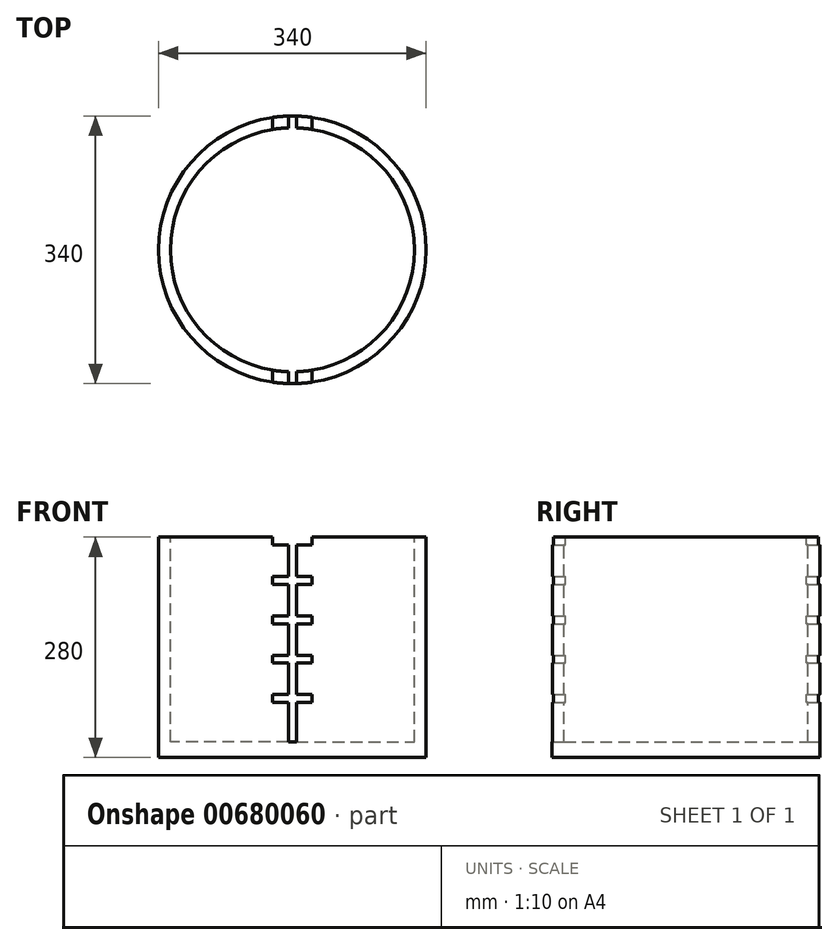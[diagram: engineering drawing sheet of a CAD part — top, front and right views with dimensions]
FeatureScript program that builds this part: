
annotation { "Feature Type Name" : "Feature", "Feature Type Description" : "" }
export const myFeature = defineFeature(function(context is Context, id is Id, definition is map)
    precondition{}
    {
        {
            var Q0;
            Q0=qCreatedBy(makeId("Top.planeOp"),FACE);
            var sketch = newSketch(context, id + "F0", { "sketchPlane" : qUnion([Q0])});
            skCircle(sketch, "E0", {"center": v(0, 0) * mm, "radius": 170 * mm});
            skSolve(sketch);
        }
        {
            var Q0;
            Q0=qSketchRegion(id+"F0",true);
            extrude(context, id + "F1", {"entities" : qUnion([Q0]), "depth" : 280 * mm});
        }
        {
            var Q0;
            Q0=makeQuery(id+"F1.opExtrude","CAP_FACE",FACE,{"disambiguationData":[OSD([sQuery(id+"F0.wireOp",EDGE,"E0")])],"isStart":false});
            var sketch = newSketch(context, id + "F2", { "sketchPlane" : qUnion([Q0])});
            skCircle(sketch, "E1", {"center": v(0, 0) * mm, "radius": 155 * mm});
            skSolve(sketch);
        }
        {
            var Q0;
            Q0=makeQuery(id+"F2.imprint","IMPRINT",FACE,{"disambiguationData":[TD([[makeQuery(id+"F2.imprint","IMPRINT",EDGE,{"derivedFrom":sQuery(id+"F2.wireOp",EDGE,"E1")}),1.0]])]});
            extrude(context, id + "F3", {"entities" : qUnion([Q0]), "operationType" : NewBodyOperationType.REMOVE, "oppositeDirection" : true, "depth" : 260 * mm});
        }
        {
            var Q0;
            Q0=qCreatedBy(makeId("Front.planeOp"),FACE);
            var sketch = newSketch(context, id + "F4", { "sketchPlane" : qUnion([Q0])});
            skLineSegment(sketch, "E2", {"start": v(0, 280) * mm, "end": v(5, 280) * mm});
            skLineSegment(sketch, "E3", {"start": v(5, 270) * mm, "end": v(5, 230) * mm});
            skLineSegment(sketch, "E4", {"start": v(5, 280) * mm, "end": v(-5, 280) * mm});
            skLineSegment(sketch, "E5", {"start": v(25, 70) * mm, "end": v(25, 80) * mm});
            skPoint(sketch, "E6.start.orphan", {"position": v(-67.32, 75) * mm});
            skLineSegment(sketch, "E7.trimOffspring", {"start": v(-5, 30) * mm, "end": v(-5, 70) * mm});
            skLineSegment(sketch, "E8", {"start": v(-25, 75) * mm, "end": v(-25, 80) * mm});
            skLineSegment(sketch, "E9", {"start": v(-25, 80) * mm, "end": v(-5, 80) * mm});
            skLineSegment(sketch, "E10", {"start": v(25, 80) * mm, "end": v(25, 70) * mm});
            skLineSegment(sketch, "E11", {"start": v(25, 70) * mm, "end": v(5, 70) * mm});
            skLineSegment(sketch, "E12.trimOffspring", {"start": v(5, 70) * mm, "end": v(5, 30) * mm});
            skLineSegment(sketch, "E13.trimOffspring", {"start": v(-5, 80) * mm, "end": v(-5, 120) * mm});
            skLineSegment(sketch, "E14", {"start": v(-25, 125) * mm, "end": v(-25, 130) * mm});
            skLineSegment(sketch, "E15", {"start": v(-25, 130) * mm, "end": v(-5, 130) * mm});
            skLineSegment(sketch, "E16", {"start": v(25, 130) * mm, "end": v(25, 120) * mm});
            skLineSegment(sketch, "E17", {"start": v(25, 120) * mm, "end": v(5, 120) * mm});
            skLineSegment(sketch, "E18.trimOffspring", {"start": v(-5, 130) * mm, "end": v(-5, 170) * mm});
            skLineSegment(sketch, "E19.trimOffspring", {"start": v(5, 120) * mm, "end": v(5, 80) * mm});
            skLineSegment(sketch, "E20.trimOffspring", {"start": v(-5, 120) * mm, "end": v(-25, 120) * mm});
            skLineSegment(sketch, "E21.trimOffspring", {"start": v(-25, 120) * mm, "end": v(-25, 130) * mm});
            skLineSegment(sketch, "E22.trimOffspring", {"start": v(25, 120) * mm, "end": v(25, 130) * mm});
            skLineSegment(sketch, "E23.trimOffspring", {"start": v(-25, 70) * mm, "end": v(-25, 80) * mm});
            skLineSegment(sketch, "E24.trimOffspring", {"start": v(-5, 70) * mm, "end": v(-25, 70) * mm});
            skLineSegment(sketch, "E25.trimOffspring", {"start": v(5, 80) * mm, "end": v(25, 80) * mm});
            skLineSegment(sketch, "E26", {"start": v(-25, 175) * mm, "end": v(-25, 180) * mm});
            skLineSegment(sketch, "E27", {"start": v(-25, 180) * mm, "end": v(-5, 180) * mm});
            skLineSegment(sketch, "E28", {"start": v(25, 180) * mm, "end": v(25, 170) * mm});
            skLineSegment(sketch, "E29", {"start": v(25, 170) * mm, "end": v(5, 170) * mm});
            skLineSegment(sketch, "E30.trimOffspring", {"start": v(-25, 170) * mm, "end": v(-25, 180) * mm});
            skLineSegment(sketch, "E31.trimOffspring", {"start": v(25, 170) * mm, "end": v(25, 180) * mm});
            skLineSegment(sketch, "E32.trimOffspring", {"start": v(5, 170) * mm, "end": v(5, 130) * mm});
            skLineSegment(sketch, "E33.trimOffspring", {"start": v(-5, 180) * mm, "end": v(-5, 220) * mm});
            skLineSegment(sketch, "E34.trimOffspring", {"start": v(5, 130) * mm, "end": v(25, 130) * mm});
            skLineSegment(sketch, "E35.trimOffspring", {"start": v(-5, 170) * mm, "end": v(-25, 170) * mm});
            skLineSegment(sketch, "E36.trimOffspring", {"start": v(5, 180) * mm, "end": v(25, 180) * mm});
            skLineSegment(sketch, "E37", {"start": v(-25, 225) * mm, "end": v(-25, 230) * mm});
            skLineSegment(sketch, "E38", {"start": v(-25, 230) * mm, "end": v(-5, 230) * mm});
            skLineSegment(sketch, "E39", {"start": v(25, 230) * mm, "end": v(25, 220) * mm});
            skLineSegment(sketch, "E40", {"start": v(25, 220) * mm, "end": v(5, 220) * mm});
            skLineSegment(sketch, "E41.trimOffspring", {"start": v(-25, 220) * mm, "end": v(-25, 230) * mm});
            skLineSegment(sketch, "E42.trimOffspring", {"start": v(25, 220) * mm, "end": v(25, 230) * mm});
            skLineSegment(sketch, "E43.trimOffspring", {"start": v(5, 220) * mm, "end": v(5, 180) * mm});
            skLineSegment(sketch, "E44.trimOffspring", {"start": v(-5, 230) * mm, "end": v(-5, 270) * mm});
            skLineSegment(sketch, "E45.trimOffspring", {"start": v(-5, 220) * mm, "end": v(-25, 220) * mm});
            skLineSegment(sketch, "E46.trimOffspring", {"start": v(5, 230) * mm, "end": v(25, 230) * mm});
            skLineSegment(sketch, "E47", {"start": v(-5, 20) * mm, "end": v(5, 20) * mm});
            skLineSegment(sketch, "E48", {"start": v(-5, 30) * mm, "end": v(-5, 20) * mm});
            skLineSegment(sketch, "E49", {"start": v(5, 30) * mm, "end": v(5, 20) * mm});
            skLineSegment(sketch, "E50", {"start": v(25, 270) * mm, "end": v(5, 270) * mm});
            skLineSegment(sketch, "E51", {"start": v(-25, 270) * mm, "end": v(-25, 280) * mm});
            skLineSegment(sketch, "E52", {"start": v(25, 270) * mm, "end": v(25, 280) * mm});
            skLineSegment(sketch, "E53", {"start": v(25, 280) * mm, "end": v(-25, 280) * mm});
            skLineSegment(sketch, "E54.trimOffspring", {"start": v(-5, 270) * mm, "end": v(-25, 270) * mm});
            skSolve(sketch);
        }
        {
            var Q0;
            Q0=qSketchRegion(id+"F4",true);
            extrude(context, id + "F5", {"entities" : qUnion([Q0]), "operationType" : NewBodyOperationType.REMOVE, "endBound" : BoundingType.THROUGH_ALL, "depth" : 25 * mm, "hasSecondDirection" : true, "secondDirectionBound" : SecondDirectionBoundingType.THROUGH_ALL, "secondDirectionOppositeDirection" : true, "secondDirectionDepth" : 25 * mm});
        }
    });
